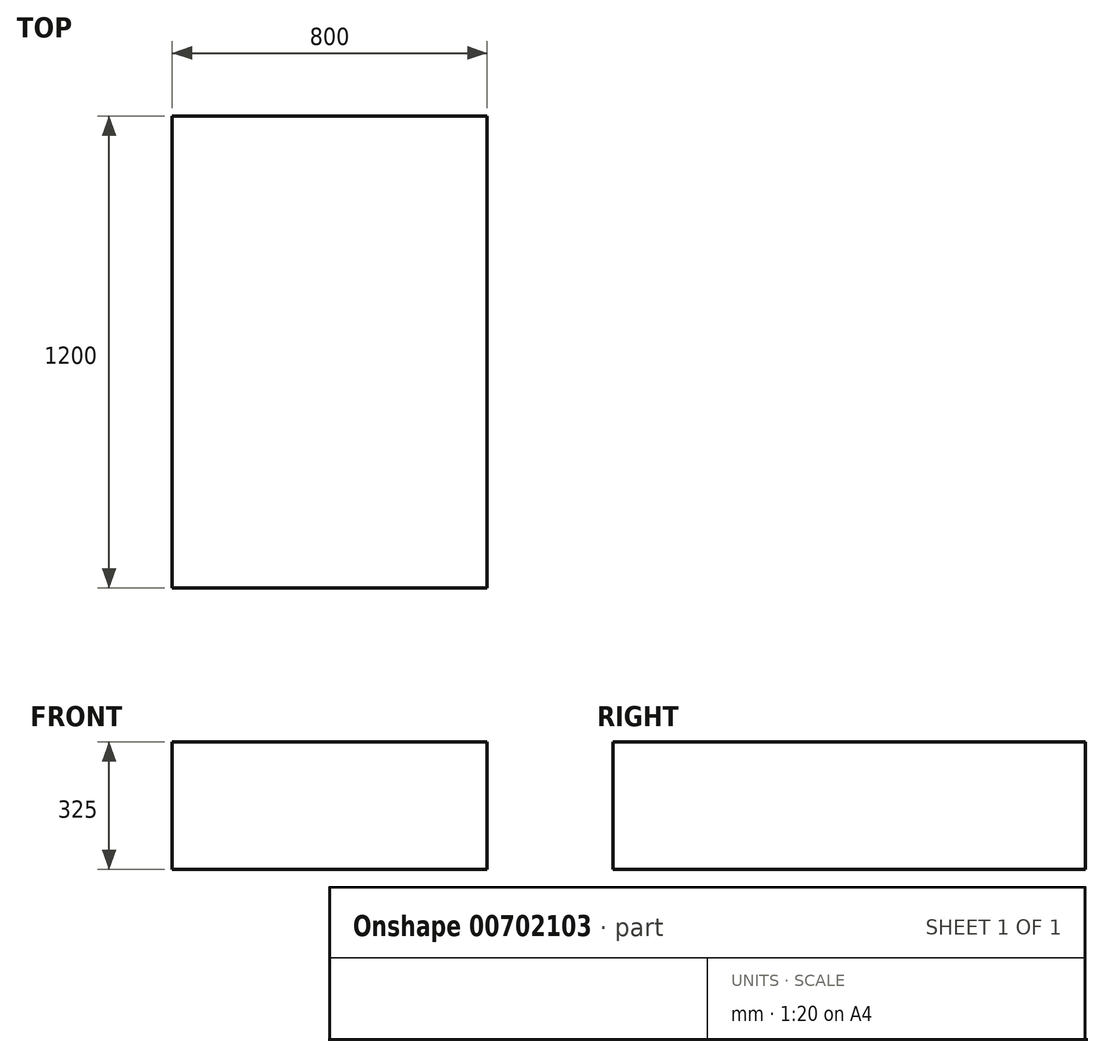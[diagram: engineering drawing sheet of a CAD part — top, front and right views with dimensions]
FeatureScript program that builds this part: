
annotation { "Feature Type Name" : "Feature", "Feature Type Description" : "" }
export const myFeature = defineFeature(function(context is Context, id is Id, definition is map)
    precondition{}
    {
        {
            var Q0;
            Q0=qCreatedBy(makeId("Top.planeOp"),FACE);
            var sketch = newSketch(context, id + "F0", { "sketchPlane" : qUnion([Q0])});
            skLineSegment(sketch, "E0.bottom", {"start": v(0, 0) * mm, "end": v(800, 0) * mm});
            skLineSegment(sketch, "E0.top", {"start": v(0, 1200) * mm, "end": v(800, 1200) * mm});
            skLineSegment(sketch, "E0.left", {"start": v(0, 0) * mm, "end": v(0, 1200) * mm});
            skLineSegment(sketch, "E0.right", {"start": v(800, 0) * mm, "end": v(800, 1200) * mm});
            skSolve(sketch);
        }
        {
            var Q0;
            Q0=makeQuery(id+"F0.imprint","IMPRINT",FACE,{"disambiguationData":[TD([[makeQuery(id+"F0.imprint","IMPRINT",EDGE,{"derivedFrom":sQuery(id+"F0.wireOp",EDGE,"E0.bottom")}),1.0]])]});
            extrude(context, id + "F1", {"entities" : qUnion([Q0]), "depth" : 325 * mm, "offsetDistance" : 25 * mm});
        }
    });
